# Revit family: Gira_215004
name_source: partatom
category: Elektroinstallationen
revit_build: Autodesk Revit 2017 (Build: 20160225_1515(x64)
units: mm (PartAtom-declared; Revit-internal decimal feet)

## family parameters
Basisbauteil = Fläche
Beim Laden mit Abzugskörper schneiden = Nein
Bemaßung runder Anschluss = Durchmesser verwenden
Beschriftungsausrichtung beibehalten = Nein
Gemeinsam genutzt = Nein
Raumberechnungspunkt = Nein
Teiletyp = Normal

## types (1)
- Gira_215004
    Akustisches Signal = Nein
    Analogeingang = Nein
    Andere Bussysteme = sonstige
    Ausführung = sonstige
    BIM = https://media.stage.bim.site
    Beschreibung = KNX Wetterstation Standard   Merkmale: - Wetterstation Standard zur Messung und Auswertung von Wetterdaten (Windgeschwindigkeit, Niederschlag, Dämmerung, Temperatur und Helligkeit). - Montage im Außenbereich von Gebäuden, vorzugsweise im Dachbereich. - Temperatursensor zur Messung der Außentemperatur. - Windsensor (thermisch) zur ermittelt die Windgeschwindigkeit. - Dämmerungssensor zur Messung der Helligkeit im Dämmerungsbereich. - Drei um 90 versetzte Helligkeitssensoren ermitteln die Helligkeit bei Tageslicht und Sonnenschein, richtungsabhängig. - Regensensor zur Erfassung des Niederschlags. - Eine Teach-in-Funktion ermöglicht das Übernehmen eines aktuellen Messwerts als Grenzwert. Dies kann z. B. per Tastendruck mit einem externen Tasters ausgelöst werden. - Zwei Grenzwerte mit einstellbarer Hysterese pro Sensor (außer Regensensor) können parametriert werden. - Alle Grenzwertobjekte haben eine parametrierbare Ein- und Ausschaltverzögerung. - Sechs Logikgatter (UND, UND mit Rückführung, ODER, Exklusiv-ODER, NAND, NOR) mit bis zu vier Eingängen für externe und interne 1 Bit Werte. - Vier Sperrglieder zum Sperren von Funktionen oder manueller Bedienung. - Zyklischen Senden bei Wertänderung.  Hinweise : - Direkte Sonneneinstrahlung kann die Temperaturmessung beeinflussen.
    Bussystem Funkbus = Nein
    Bussystem KNX = Ja
    Bussystem KNX-Funk = Nein
    Bussystem LON = Nein
    Bussystem Powernet = Nein
    Datenblatt = https://katalog.gira.de
    Farbe = Aluminium
    GTIN = 4010337058441
    HAN = 215004
    Hersteller = Gira
    Mit Busankopplung = Nein
    Mit DCF77 = Nein
    Mit Heizung = Nein
    Montageart = Aufputz
    Produktseite = http://katalog.gira.de
    Schutzart (IP) = IP44
    Typname = Wetterstation Standard KNX
    URL = https://www.gira.de
    Vorgabe-Ansicht = 1219 mm
    Wetterstation = Nein

## geometry (parser evidence)
native form markers: Sweep x1
no freeform markers — native parametric forms only
